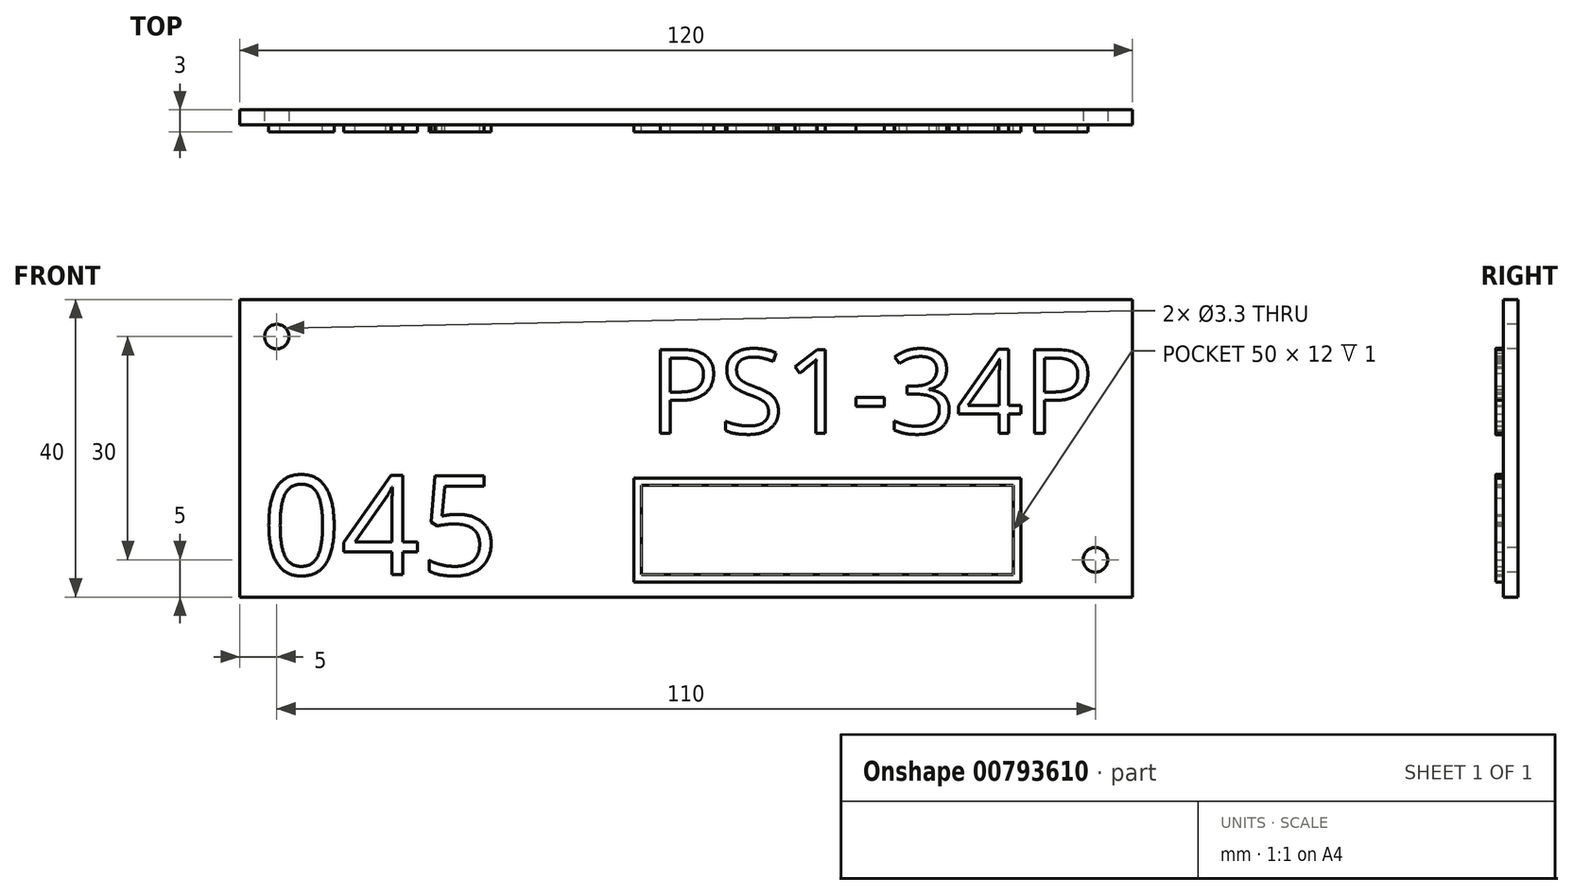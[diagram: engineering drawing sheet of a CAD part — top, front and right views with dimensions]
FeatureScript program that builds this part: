
annotation { "Feature Type Name" : "Feature", "Feature Type Description" : "" }
export const myFeature = defineFeature(function(context is Context, id is Id, definition is map)
    precondition{}
    {
        {
            var Q0;
            Q0=qCreatedBy(makeId("Front.planeOp"),FACE);
            var sketch = newSketch(context, id + "F0", { "sketchPlane" : qUnion([Q0])});
            skLineSegment(sketch, "E0.bottom", {"start": v(60, -20) * mm, "end": v(-60, -20) * mm});
            skLineSegment(sketch, "E0.top", {"start": v(60, 20) * mm, "end": v(-60, 20) * mm});
            skLineSegment(sketch, "E0.left", {"start": v(60, -20) * mm, "end": v(60, 20) * mm});
            skLineSegment(sketch, "E0.right", {"start": v(-60, -20) * mm, "end": v(-60, 20) * mm});
            skPoint(sketch, "E0.middle", {"position": v(0, 0) * mm});
            skSolve(sketch);
        }
        {
            var Q0;
            Q0=makeQuery(id+"F0.imprint","IMPRINT",FACE,{"disambiguationData":[TD([[makeQuery(id+"F0.imprint","IMPRINT",EDGE,{"derivedFrom":sQuery(id+"F0.wireOp",EDGE,"E0.bottom")}),-1.0]])]});
            extrude(context, id + "F1", {"entities" : qUnion([Q0]), "depth" : 2 * mm});
        }
        {
            var Q0;
            Q0=makeQuery(id+"F1.opExtrude","CAP_FACE",FACE,{"disambiguationData":[OSD([sQuery(id+"F0.wireOp",EDGE,"E0.bottom"),sQuery(id+"F0.wireOp",EDGE,"E0.top"),sQuery(id+"F0.wireOp",EDGE,"E0.left"),sQuery(id+"F0.wireOp",EDGE,"E0.right")])],"isStart":false});
            var sketch = newSketch(context, id + "F2", { "sketchPlane" : qUnion([Q0])});
            skPoint(sketch, "E1", {"position": v(-55, 15) * mm});
            skPoint(sketch, "E2", {"position": v(55, -15) * mm});
            skSolve(sketch);
        }
        {
            var Q0;
            Q0=sQuery(id+"F2.wireOp",VERTEX,"E1");
            var Q1;
            Q1=sQuery(id+"F2.wireOp",VERTEX,"E2");
            var Q2;
            Q2=makeQuery(id+"F1.opExtrude","SWEPT_BODY",BODY,{"disambiguationData":[OSD([sQuery(id+"F0.wireOp",EDGE,"E0.bottom"),sQuery(id+"F0.wireOp",EDGE,"E0.top"),sQuery(id+"F0.wireOp",EDGE,"E0.left"),sQuery(id+"F0.wireOp",EDGE,"E0.right")])]});
            hole(context, id + "F3", {"style" : HoleStyle.SIMPLE, "endStyle" : HoleEndStyle.THROUGH, "holeDiameter" : 3.3 * mm, "locations" : qUnion([Q0, Q1]), "scope" : qUnion([Q2]), "isTappedThrough" : true});
        }
        {
            var Q0;
            Q0=makeQuery(id+"F1.opExtrude","CAP_FACE",FACE,{"disambiguationData":[OSD([sQuery(id+"F0.wireOp",EDGE,"E0.bottom"),sQuery(id+"F0.wireOp",EDGE,"E0.top"),sQuery(id+"F0.wireOp",EDGE,"E0.left"),sQuery(id+"F0.wireOp",EDGE,"E0.right")])],"isStart":false});
            var sketch = newSketch(context, id + "F4", { "sketchPlane" : qUnion([Q0])});
            skText(sketch, "E3", { "text": "PS1-34P", "fontName": "OpenSans-Regular.ttf"});
            const initialGuessF4  = {"E3": [-0.005, 0.002, 1, 0, 0.01136]};
            skSetInitialGuess(sketch, initialGuessF4);
            skSolve(sketch);
        }
        {
            var Q0;
            Q0=qSketchRegion(id+"F4",true);
            extrude(context, id + "F5", {"entities" : qUnion([Q0]), "operationType" : NewBodyOperationType.ADD, "depth" : 1 * mm});
        }
        {
            var Q0;
            {var subQ0=sQuery(id+"F0.wireOp",EDGE,"E0.top");var subQ1=sQuery(id+"F0.wireOp",EDGE,"E0.left");var subQ2=sQuery(id+"F0.wireOp",EDGE,"E0.right");var subQ3=sQuery(id+"F0.wireOp",EDGE,"E0.bottom");Q0=makeQuery(id+"F5.boolean.opBoolean","SPLIT",FACE,{"disambiguationData":[TD([makeQuery(id+"F1.opExtrude","SWEPT_FACE",FACE,{"disambiguationData":[OSD([subQ3])]})])],"derivedFrom":makeQuery(id+"F1.opExtrude","CAP_FACE",FACE,{"disambiguationData":[OSD([subQ3,subQ0,subQ1,subQ2])],"isStart":false})});}
            var sketch = newSketch(context, id + "F6", { "sketchPlane" : qUnion([Q0])});
            skText(sketch, "E4", { "text": "045", "fontName": "OpenSans-Regular.ttf"});
            const initialGuessF6  = {"E4": [-0.057, -0.017, 1, 0, 0.01338]};
            skSetInitialGuess(sketch, initialGuessF6);
            skSolve(sketch);
        }
        {
            var Q0;
            Q0=qSketchRegion(id+"F6",true);
            extrude(context, id + "F7", {"entities" : qUnion([Q0]), "operationType" : NewBodyOperationType.ADD, "depth" : 1 * mm});
        }
        {
            var Q0;
            {var subQ46=sQuery(id+"F0.wireOp",EDGE,"E0.top");var subQ48=sQuery(id+"F0.wireOp",EDGE,"E0.left");var subQ66=sQuery(id+"F0.wireOp",EDGE,"E0.right");var subQ76=sQuery(id+"F0.wireOp",EDGE,"E0.bottom");var subQ77=makeQuery(id+"F1.opExtrude","SWEPT_FACE",FACE,{"disambiguationData":[OSD([subQ76])]});Q0=makeQuery(id+"F7.boolean.opBoolean","SPLIT",FACE,{"disambiguationData":[TD([subQ77])],"derivedFrom":makeQuery(id+"F5.boolean.opBoolean","SPLIT",FACE,{"disambiguationData":[TD([subQ77])],"derivedFrom":makeQuery(id+"F1.opExtrude","CAP_FACE",FACE,{"disambiguationData":[OSD([subQ76,subQ46,subQ48,subQ66])],"isStart":false})})});}
            var sketch = newSketch(context, id + "F8", { "sketchPlane" : qUnion([Q0])});
            skLineSegment(sketch, "E5.bottom", {"start": v(45, -18) * mm, "end": v(-7, -18) * mm});
            skLineSegment(sketch, "E5.top", {"start": v(45, -4) * mm, "end": v(-7, -4) * mm});
            skLineSegment(sketch, "E5.left", {"start": v(45, -18) * mm, "end": v(45, -4) * mm});
            skLineSegment(sketch, "E5.right", {"start": v(-7, -18) * mm, "end": v(-7, -4) * mm});
            skPoint(sketch, "E5.middle", {"position": v(19, -11) * mm});
            skLineSegment(sketch, "E6.0", {"start": v(44, -5) * mm, "end": v(-6, -5) * mm});
            skLineSegment(sketch, "E6.1", {"start": v(44, -17) * mm, "end": v(44, -5) * mm});
            skLineSegment(sketch, "E6.2", {"start": v(44, -17) * mm, "end": v(-6, -17) * mm});
            skLineSegment(sketch, "E6.3", {"start": v(-6, -17) * mm, "end": v(-6, -5) * mm});
            skSolve(sketch);
        }
        {
            var Q0;
            Q0=makeQuery(id+"F8.imprint","IMPRINT",FACE,{"disambiguationData":[TD([[makeQuery(id+"F8.imprint","IMPRINT",EDGE,{"derivedFrom":sQuery(id+"F8.wireOp",EDGE,"E5.bottom")}),-1.0]])]});
            extrude(context, id + "F9", {"entities" : qUnion([Q0]), "operationType" : NewBodyOperationType.ADD, "depth" : 1 * mm});
        }
    });
